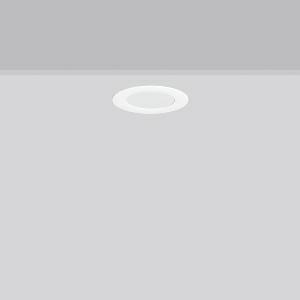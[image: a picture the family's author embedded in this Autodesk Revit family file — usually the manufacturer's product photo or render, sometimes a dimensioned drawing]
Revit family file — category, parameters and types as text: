
# Revit family: toledo_flat_round_e_672228_002_1_1e8f
name_source: partatom
category: Lighting Fixtures
units: mm (PartAtom-declared; Revit-internal decimal feet)

## family parameters
Cut with Voids When Loaded = No
Host = Face
Light Source = No
Part Type = Normal
Room Calculation Point = No
Round Connector Dimension = Use Diameter
Shared = No

## types (1)
- TOLEDO FLAT round E (1 x LED Modul 840, 530 lm, 4000)
    Apparent Load = 5 VA
    CIE Flux Codes = 48 79 96 100 100
    Color Rendering = 80
    Color Temperature = 4000
    Default Elevation = 1800 mm
    Description = Series: TOLEDO FLAT round
Ultra thin recessed downlight. For escape route illumination. Housing: die-cast aluminium, powder-coated. Lightguide and diffuser made of non-yellowing plastic (PMMA). Diffuser opal matt plastic. Ceiling installation with spring system. Including separate LED converter with connecting cable 250 mm. Suitable for connection to central battery systems. External driver with simple plug-in locking system. 
Colour: white
Diameter: 148 mm
Height: 2 mm
Cut-out diameter: 128 mm
Recess height: 35 mm
Luminaire: recess height: 31-51 mm
Weight: 293 g
Operating mode: maintained power mode
Lamp: LED
Socket: without socket
Colour temperature: 4000K
Colour rendering index (CRI): 80
System power: 5 W
Rated luminous flux: 530 lm
Luminous flux, emergency: 530 lm
System power, emergency: 5 W
Control gear: Regulated power supply
Protection class: II
Type of protection: IP 54
    Height = 0 mm  [stored 0 ft]
    Lamp = 1 x LED Modul 840
    Lamp Light Flux = 530 lm
    Lamp count = 1
    Length = 148 mm
    Lifetime = 50000 h
    Luminous efficacy = 106 lm/W
    Manufacturer = RZB
    ModVariant = No
    Model = 672228.002.1
    Mounting Place = Ceiling
    Mounting Type = Recessed
    Number of Poles = 1
    OnlyDefault = Yes
    Power Factor = 1
    Product Name = TOLEDO FLAT round E
    Product group = Recessed downlights
    ProductGroupID = 402
    Protection Class = Protection class II
    Protection Degree = IP 40
    RLX_Detail_Level = 1
    RLX_Emergency_Light_Flux = 530 lm
    RLX_Emergency_Type = 3
    RLX_Emergency_Type_DB = Yes
    RlxData = <blob elided: 27525 chars, md5=e39d1be8>
    Socket = socket
    Standby Power = 0 W
    System Light Flux = 530 lm
    System Power = 5 W
    Type Comments = Product without accessories
    Type Image = 901451.002.jpg
    URL = http://relux.com
    VarID = ---
    Voltage = 230 V
    Voltage Range = 220-240 V
    Weight = 0.00 kg
    Width = 0 mm  [stored 0 ft]

note: [stored X ft] marks values corroborated as IEEE doubles in the binary element streams (Revit-internal decimal feet)

## geometry (parser evidence)
native form markers: Blend x4, Sweep x12
no freeform markers — native parametric forms only
